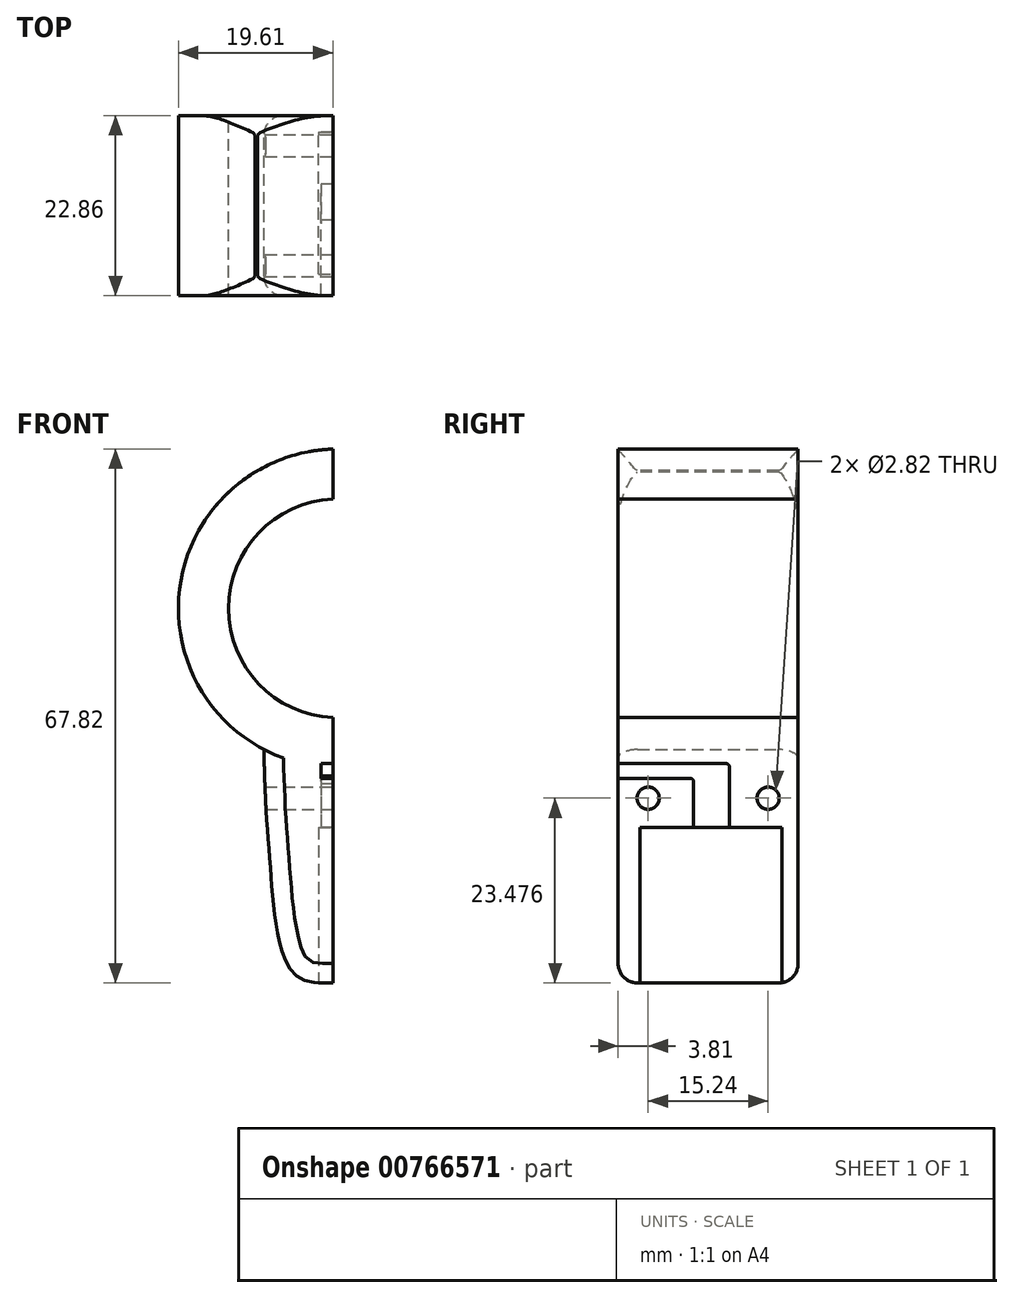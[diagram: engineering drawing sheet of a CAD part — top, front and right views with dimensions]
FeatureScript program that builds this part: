
annotation { "Feature Type Name" : "Feature", "Feature Type Description" : "" }
export const myFeature = defineFeature(function(context is Context, id is Id, definition is map)
    precondition{}
    {
        {
            var Q0;
            Q0=qCreatedBy(makeId("Front.planeOp"),FACE);
            var sketch = newSketch(context, id + "F0", { "sketchPlane" : qUnion([Q0])});
            skCircle(sketch, "E0", {"center": v(0, 0) * mm, "radius": 13.9 * mm});
            skCircle(sketch, "E1.0", {"center": v(0, 0) * mm, "radius": 20.24 * mm});
            skFitSpline(sketch, "E2", {"points": [v(-10.48, 17.32) * mm, v(-6.62, 22.45) * mm, v(-5.79, 30.49) * mm, v(0, 31.88) * mm, v(5.12, 30.56) * mm, v(6.08, 23.46) * mm, v(9.7, 17.76) * mm], "startDerivative": vector(26.15, 14.41) * mm, "endDerivative": vector(40.23, -23.63) * mm});
            skFitSpline(sketch, "E3", {"points": [v(-9.4, -17.93) * mm, v(-8.61, -32.2) * mm, v(-5.82, -46.1) * mm, v(0, -47.57) * mm, v(6.45, -45.96) * mm, v(9.7, -28.64) * mm, v(9.7, -17.76) * mm], "startDerivative": vector(4.47, -161.39) * mm, "endDerivative": vector(-1.33, 64.22) * mm});
            skSolve(sketch);
        }
        {
            var Q0;
            Q0=makeQuery(id+"F0.imprint","IMPRINT",FACE,{"disambiguationData":[TD([[makeQuery(id+"F0.imprint","IMPRINT",EDGE,{"derivedFrom":sQuery(id+"F0.wireOp",EDGE,"E0")}),-1.0]])]});
            var Q1;
            {var subQ0=sQuery(id+"F0.wireOp",EDGE,"E3");Q1=makeQuery(id+"F0.imprint","IMPRINT",FACE,{"disambiguationData":[TD([[makeQuery(id+"F0.imprint","IMPRINT",EDGE,{"derivedFrom":subQ0}),1.0]])]});}
            var Q2;
            {var subQ0=sQuery(id+"F0.wireOp",EDGE,"E2");var subQ1=sQuery(id+"F0.wireOp",EDGE,"E1.0");var subQ2=makeQuery(id+"F0.imprint","INTERSECT",VERTEX,{"disambiguationData":[OD(1.0)],"derivedFrom":[subQ1,subQ0]});Q2=makeQuery(id+"F0.imprint","IMPRINT",FACE,{"disambiguationData":[TD([[makeQuery(id+"F0.imprint","IMPRINT",EDGE,{"disambiguationData":[TD([[subQ2,-1.0]])],"derivedFrom":subQ1}),-1.0]])]});}
            extrude(context, id + "F1", {"entities" : qUnion([Q0, Q1, Q2]), "depth" : 22.86 * mm, "offsetDistance" : 25.4 * mm});
        }
        {
            var Q0;
            Q0=qCreatedBy(makeId("Right.planeOp"),FACE);
            var sketch = newSketch(context, id + "F2", { "sketchPlane" : qUnion([Q0])});
            skCircle(sketch, "E4", {"center": v(-10.97, 26.33) * mm, "radius": 1.9 * mm});
            skCircle(sketch, "E5", {"center": v(-19.05, -24.11) * mm, "radius": 1.41 * mm});
            skCircle(sketch, "E6", {"center": v(-3.81, -24.11) * mm, "radius": 1.41 * mm});
            skSolve(sketch);
        }
        {
            var Q0;
            Q0=qSketchRegion(id+"F2",true);
            extrude(context, id + "F3", {"entities" : qUnion([Q0]), "operationType" : NewBodyOperationType.REMOVE, "endBound" : BoundingType.SYMMETRIC, "oppositeDirection" : true, "depth" : 25.4 * mm, "offsetDistance" : 25.4 * mm});
        }
        {
            var Q0;
            Q0=qCreatedBy(makeId("Front.planeOp"),FACE);
            var sketch = newSketch(context, id + "F4", { "sketchPlane" : qUnion([Q0])});
            skLineSegment(sketch, "E7.bottom", {"start": v(-0.64, 36.94) * mm, "end": v(30.33, 36.94) * mm});
            skLineSegment(sketch, "E7.top", {"start": v(-0.64, -50.47) * mm, "end": v(30.33, -50.47) * mm});
            skLineSegment(sketch, "E7.left", {"start": v(-0.64, 36.94) * mm, "end": v(-0.64, -50.47) * mm});
            skLineSegment(sketch, "E7.right", {"start": v(30.33, 36.94) * mm, "end": v(30.33, -50.47) * mm});
            skSolve(sketch);
        }
        {
            var Q0;
            Q0=makeQuery(id+"F4.imprint","IMPRINT",FACE,{"disambiguationData":[TD([[makeQuery(id+"F4.imprint","IMPRINT",EDGE,{"derivedFrom":sQuery(id+"F4.wireOp",EDGE,"E7.bottom")}),-1.0]])]});
            extrude(context, id + "F5", {"entities" : qUnion([Q0]), "operationType" : NewBodyOperationType.REMOVE, "depth" : 25.4 * mm, "offsetDistance" : 25.4 * mm});
        }
        {
            var Q0;
            Q0=makeQuery(id+"F1.opExtrude","CAP_EDGE",EDGE,{"disambiguationData":[OSD([sQuery(id+"F0.wireOp",EDGE,"E2")])],"isStart":false});
            var Q1;
            {var subQ0=sQuery(id+"F0.wireOp",EDGE,"E1.0");Q1=makeQuery(id+"F1.opExtrude","CAP_EDGE",EDGE,{"disambiguationData":[OSD([subQ0]),TDD([makeQuery(id+"F0.imprint","IMPRINT",EDGE,{"disambiguationData":[TD([[makeQuery(id+"F0.imprint","INTERSECT",VERTEX,{"disambiguationData":[OD(0.0)],"derivedFrom":[subQ0,sQuery(id+"F0.wireOp",EDGE,"E2")]}),-1.0]])],"derivedFrom":subQ0})])],"isStart":false});}
            var Q2;
            Q2=makeQuery(id+"F1.opExtrude","CAP_EDGE",EDGE,{"disambiguationData":[OSD([sQuery(id+"F0.wireOp",EDGE,"E3")])],"isStart":false});
            var Q3;
            Q3=makeQuery(id+"F1.opExtrude","CAP_EDGE",EDGE,{"disambiguationData":[OSD([sQuery(id+"F0.wireOp",EDGE,"E2")])],"isStart":true});
            var Q4;
            {var subQ0=sQuery(id+"F0.wireOp",EDGE,"E1.0");Q4=makeQuery(id+"F1.opExtrude","CAP_EDGE",EDGE,{"disambiguationData":[OSD([subQ0]),TDD([makeQuery(id+"F0.imprint","IMPRINT",EDGE,{"disambiguationData":[TD([[makeQuery(id+"F0.imprint","INTERSECT",VERTEX,{"disambiguationData":[OD(0.0)],"derivedFrom":[subQ0,sQuery(id+"F0.wireOp",EDGE,"E2")]}),-1.0]])],"derivedFrom":subQ0})])],"isStart":true});}
            var Q5;
            Q5=makeQuery(id+"F1.opExtrude","CAP_EDGE",EDGE,{"disambiguationData":[OSD([sQuery(id+"F0.wireOp",EDGE,"E3")])],"isStart":true});
            fillet(context, id + "F6", {"entities" : qUnion([Q0, Q1, Q2, Q3, Q4, Q5]), "radius" : 2.45 * mm, "tangentPropagation" : true, "allowEdgeOverflow" : false});
        }
        {
            var Q0;
            {var subQ1=sQuery(id+"F0.wireOp",EDGE,"E3");Q0=makeQuery(id+"F5.boolean.opBoolean","COPY",FACE,{"disambiguationData":[TD([makeQuery(id+"F1.opExtrude","SWEPT_FACE",FACE,{"disambiguationData":[OSD([subQ1])]})])],"derivedFrom":makeQuery(id+"F5.opExtrude","SWEPT_FACE",FACE,{"disambiguationData":[OSD([sQuery(id+"F4.wireOp",EDGE,"E7.left")])]})});}
            var sketch = newSketch(context, id + "F7", { "sketchPlane" : qUnion([Q0])});
            skLineSegment(sketch, "E8.bottom", {"start": v(-20.1, -27.85) * mm, "end": v(-2.07, -27.85) * mm});
            skLineSegment(sketch, "E8.top", {"start": v(-20.1, -50.8) * mm, "end": v(-2.07, -50.8) * mm});
            skLineSegment(sketch, "E8.left", {"start": v(-20.1, -27.85) * mm, "end": v(-20.1, -50.8) * mm});
            skLineSegment(sketch, "E8.right", {"start": v(-2.07, -27.85) * mm, "end": v(-2.07, -50.8) * mm});
            skSolve(sketch);
        }
        {
            var Q0;
            {var subQ0=sQuery(id+"F7.wireOp",EDGE,"E8.bottom");Q0=makeQuery(id+"F7.imprint","IMPRINT",FACE,{"disambiguationData":[TD([[makeQuery(id+"F7.imprint","IMPRINT",EDGE,{"derivedFrom":subQ0}),-1.0]])]});}
            var Q1;
            {var subQ0=sQuery(id+"F7.wireOp",EDGE,"E8.top");Q1=makeQuery(id+"F7.imprint","IMPRINT",FACE,{"disambiguationData":[TD([[makeQuery(id+"F7.imprint","IMPRINT",EDGE,{"derivedFrom":subQ0}),1.0]])]});}
            extrude(context, id + "F8", {"entities" : qUnion([Q0, Q1]), "operationType" : NewBodyOperationType.REMOVE, "oppositeDirection" : true, "depth" : 1.78 * mm, "offsetDistance" : 25.4 * mm});
        }
        {
            var Q0;
            {var subQ1=sQuery(id+"F0.wireOp",EDGE,"E3");Q0=makeQuery(id+"F5.boolean.opBoolean","COPY",FACE,{"disambiguationData":[TD([makeQuery(id+"F1.opExtrude","SWEPT_FACE",FACE,{"disambiguationData":[OSD([subQ1])]})])],"derivedFrom":makeQuery(id+"F5.opExtrude","SWEPT_FACE",FACE,{"disambiguationData":[OSD([sQuery(id+"F4.wireOp",EDGE,"E7.left")])]})});}
            var sketch = newSketch(context, id + "F9", { "sketchPlane" : qUnion([Q0])});
            skLineSegment(sketch, "E9.top", {"start": v(-13.28, -31.32) * mm, "end": v(-8.7, -31.32) * mm});
            skLineSegment(sketch, "E9.left", {"start": v(-13.28, -22.26) * mm, "end": v(-13.28, -31.32) * mm});
            skLineSegment(sketch, "E9.right", {"start": v(-8.7, -21.27) * mm, "end": v(-8.7, -31.32) * mm});
            skLineSegment(sketch, "E10.right", {"start": v(-23.82, -19.72) * mm, "end": v(-23.82, -21.6) * mm});
            skLineSegment(sketch, "E11", {"start": v(-23.82, -21.6) * mm, "end": v(-13.7, -21.6) * mm});
            skLineSegment(sketch, "E12", {"start": v(-23.82, -19.72) * mm, "end": v(-9.14, -19.72) * mm});
            skLineSegment(sketch, "E13", {"start": v(-8.7, -21.27) * mm, "end": v(-8.73, -20.13) * mm});
            skLineSegment(sketch, "E14", {"start": v(-13.28, -22.02) * mm, "end": v(-13.28, -22.26) * mm});
            skPoint(sketch, "E15.visualSharp", {"position": v(-8.73, -19.72) * mm});
            skArc(sketch, "E15.filletArc", {"start": v(-8.73, -20.13) * mm, "mid": v(-8.85, -19.84) * mm, "end": v(-9.14, -19.72) * mm});
            skPoint(sketch, "E16.visualSharp", {"position": v(-13.29, -21.6) * mm});
            skArc(sketch, "E16.filletArc", {"start": v(-13.28, -22.02) * mm, "mid": v(-13.4, -21.73) * mm, "end": v(-13.7, -21.6) * mm});
            skSolve(sketch);
        }
        {
            var Q0;
            {var subQ1=sQuery(id+"F9.wireOp",EDGE,"E9.bottom");Q0=makeQuery(id+"F9.imprint","IMPRINT",FACE,{"disambiguationData":[TD([[makeQuery(id+"F9.imprint","IMPRINT",EDGE,{"derivedFrom":subQ1}),-1.0]])]});}
            var Q1;
            {var subQ0=sQuery(id+"F9.wireOp",EDGE,"E9.top");Q1=makeQuery(id+"F9.imprint","IMPRINT",FACE,{"disambiguationData":[TD([[makeQuery(id+"F9.imprint","IMPRINT",EDGE,{"derivedFrom":subQ0}),1.0]])]});}
            var Q2;
            {var subQ7=sQuery(id+"F9.wireOp",EDGE,"E13");Q2=makeQuery(id+"F9.imprint","IMPRINT",FACE,{"disambiguationData":[TD([[makeQuery(id+"F9.imprint","IMPRINT",EDGE,{"derivedFrom":subQ7}),1.0]])]});}
            extrude(context, id + "F10", {"entities" : qUnion([Q0, Q1, Q2]), "operationType" : NewBodyOperationType.REMOVE, "oppositeDirection" : true, "depth" : 1.52 * mm, "offsetDistance" : 25.4 * mm});
        }
    });
